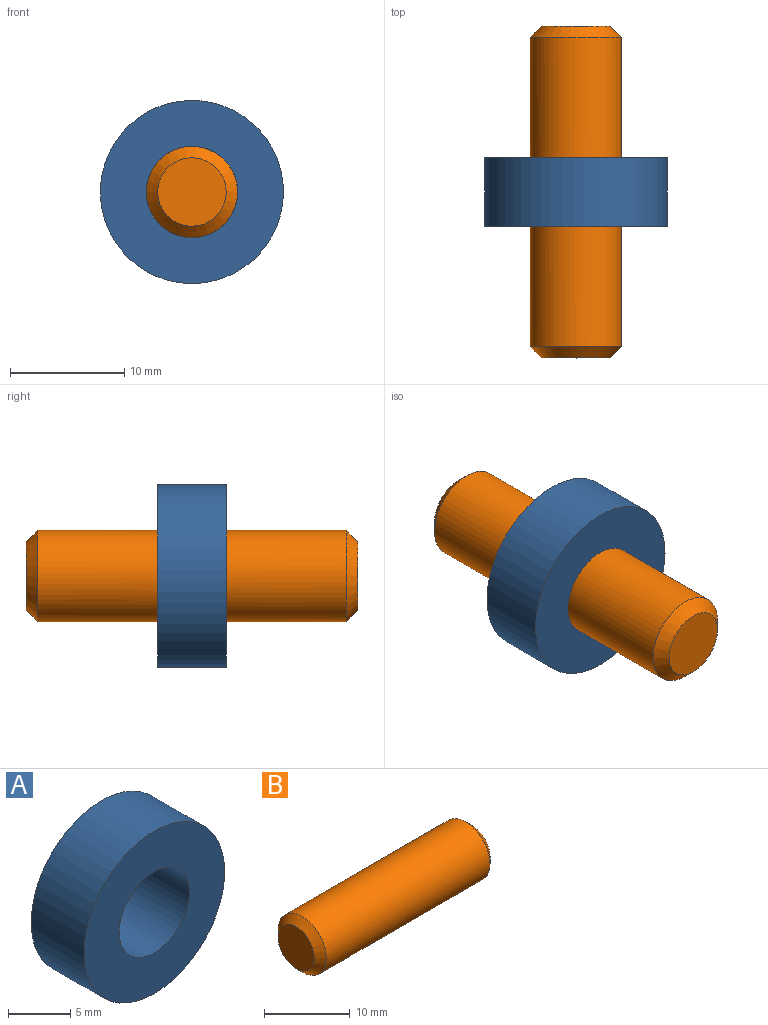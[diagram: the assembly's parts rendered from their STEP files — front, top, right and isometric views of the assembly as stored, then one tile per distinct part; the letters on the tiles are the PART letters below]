
ASSEMBLY  parts=2 mates=1
PART A: 4 faces, bbox 16x6x16 mm
  f0: cylinder r=4mm len=8mm, axis (0,1,0), area 150.8mm2, adj f2,f3
  f1: cylinder r=8mm len=16mm, axis (0,1,0), area 301.6mm2, adj f2,f3
  f2: plane 16x16mm, normal (0,-1,0), area 150.8mm2, adj f0,f1
  f3: plane 16x16mm, normal (0,1,0), area 150.8mm2, adj f0,f1
PART B: 9 faces, bbox 29x8x8 mm
  f0: cone r=3.98mm half-angle=45deg, axis (-1,0,0), area 31mm2, adj f4,f6
  f1: cone r=2.98mm half-angle=45deg, axis (1,0,0), area 31mm2, adj f4,f5
  f2: cylinder r=2.75mm len=5.74mm, axis (0,0,1), area 90mm2, adj f4,f8
  f3: cylinder r=2.75mm len=5.74mm, axis (0,0,1), area 90mm2, adj f4,f7
  f4: cylinder r=3.98mm len=27mm, axis (-1,0,0), area 625mm2, adj f0,f1,f2,f3
  f5: plane 5.97x5.97mm, normal (-1,0,0), area 28mm2, adj f1
  f6: plane 5.97x5.97mm, normal (1,0,0), area 28mm2, adj f0
  f7: plane 5.5x5.5mm, normal (0,0,-1), area 23.8mm2, adj f3
  f8: plane 5.5x5.5mm, normal (0,0,-1), area 23.8mm2, adj f2
PLACE A rot(axis=(0,-1,0),42deg) t=(-13.36,23.5,-0.08)mm
PLACE B rot(axis=(-0.34,-0.34,0.88),97.4deg) t=(-13.36,23.5,-0.08)mm
MATE fastened A.f0 <-> B.f0  axis (0,1,0) through (-13.36,23.5,-0.08)mm
